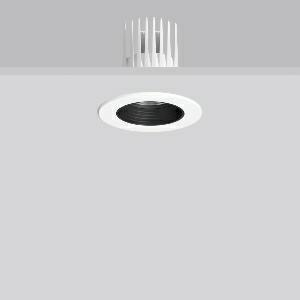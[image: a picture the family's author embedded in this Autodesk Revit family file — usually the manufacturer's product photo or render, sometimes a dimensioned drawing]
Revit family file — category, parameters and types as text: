
# Revit family: heledon_mini_e_901754_002_1_76_2386
name_source: partatom
category: Lighting Fixtures
units: mm (PartAtom-declared; Revit-internal decimal feet)

## family parameters
Cut with Voids When Loaded = No
Host = Face
Light Source = No
Part Type = Normal
Room Calculation Point = No
Round Connector Dimension = Use Diameter
Shared = No

## types (1)
- HELEDON mini E (1 x LED Modul 940, 3500 lm, 4000)
    Apparent Load = 29 VA
    Approval mark = CE
    CIE Flux Codes = 80 99 100 100 100
    Color Rendering = 92
    Color Temperature = 4000
    Default Elevation = 1800 mm
    Description = Series: HELEDON mini
Round recessed downlight. Housing: die-cast aluminium, powder-coated. Black plastic ring and recessed LED to prevent glare from the side. Optical assembly with lens made of plastic (polycarbonate) for the best homogeneous light distribution - can be changed without tools. Best colour rendering index Ra>90. Suitable for Recessed ceiling mounting. Installation without tools thanks to spring fastening system. Including separate LED converter with connecting cable 600 mm.High quality converter without flickering and stroboscopic effect. Through-wiring box (5 pole) available as accessory. The following accessories can be mounted without use of tools: interchangeable lenses, decorative glasses, honeycomb louvre, clear and frosted diffusers, white interchangeable plastic ring. 
Colour: traffic white, matt (RAL 9016)
Diameter: 124 mm
Height: 3 mm
Cut-out diameter: 114 mm
Recess height: 170 mm
Luminaire: recess height: 120 mm
Lamp: LED
Socket: without socket
Colour temperature: 4000K
Colour rendering index (CRI): 92
System power: 29 W
Rated luminous flux: 3500 lm
Luminous efficiency: 121 lm/W
Control gear: Converter, dimmable, DALI
Protection class: II
Type of protection: IP 20
    Height = 0 mm  [stored 0 ft]
    Lamp = 1 x LED Modul 940
    Lamp Light Flux = 3500 lm
    Lamp count = 1
    Length = 124 mm  [stored 0.406824 ft]
    Lifetime = 50000 h
    Luminous efficacy = 121 lm/W
    Manufacturer = RZB
    ModVariant = No
    Model = 901754.002.1.76
    Mounting Place = Ceiling
    Mounting Type = Recessed
    Number of Poles = 1
    OnlyDefault = Yes
    Power Factor = 1
    Product Name = HELEDON mini E
    Product group = Recessed downlights
    ProductGroupID = 402
    Protection Class = Protection class II
    Protection Degree = IP 20
    RLX_Detail_Level = 1
    RLX_Emergency_Light_Flux = 0 lm
    RLX_Emergency_Type = 0
    RLX_Emergency_Type_DB = No
    RlxData = <blob elided: 127369 chars, md5=48560f44>
    Socket = socket
    Standby Power = 0 W
    System Light Flux = 3500 lm
    System Power = 29 W
    Type Comments = Product without accessories
    Type Image = 901656.002.jpg
    URL = http://relux.com
    VarID = ---
    Voltage = 230 V
    Voltage Range = 220-240 V
    Weight = 0.00 kg
    Width = 0 mm  [stored 0 ft]

note: [stored X ft] marks values corroborated as IEEE doubles in the binary element streams (Revit-internal decimal feet)

## geometry (parser evidence)
native form markers: Blend x4, Sweep x12
no freeform markers — native parametric forms only
